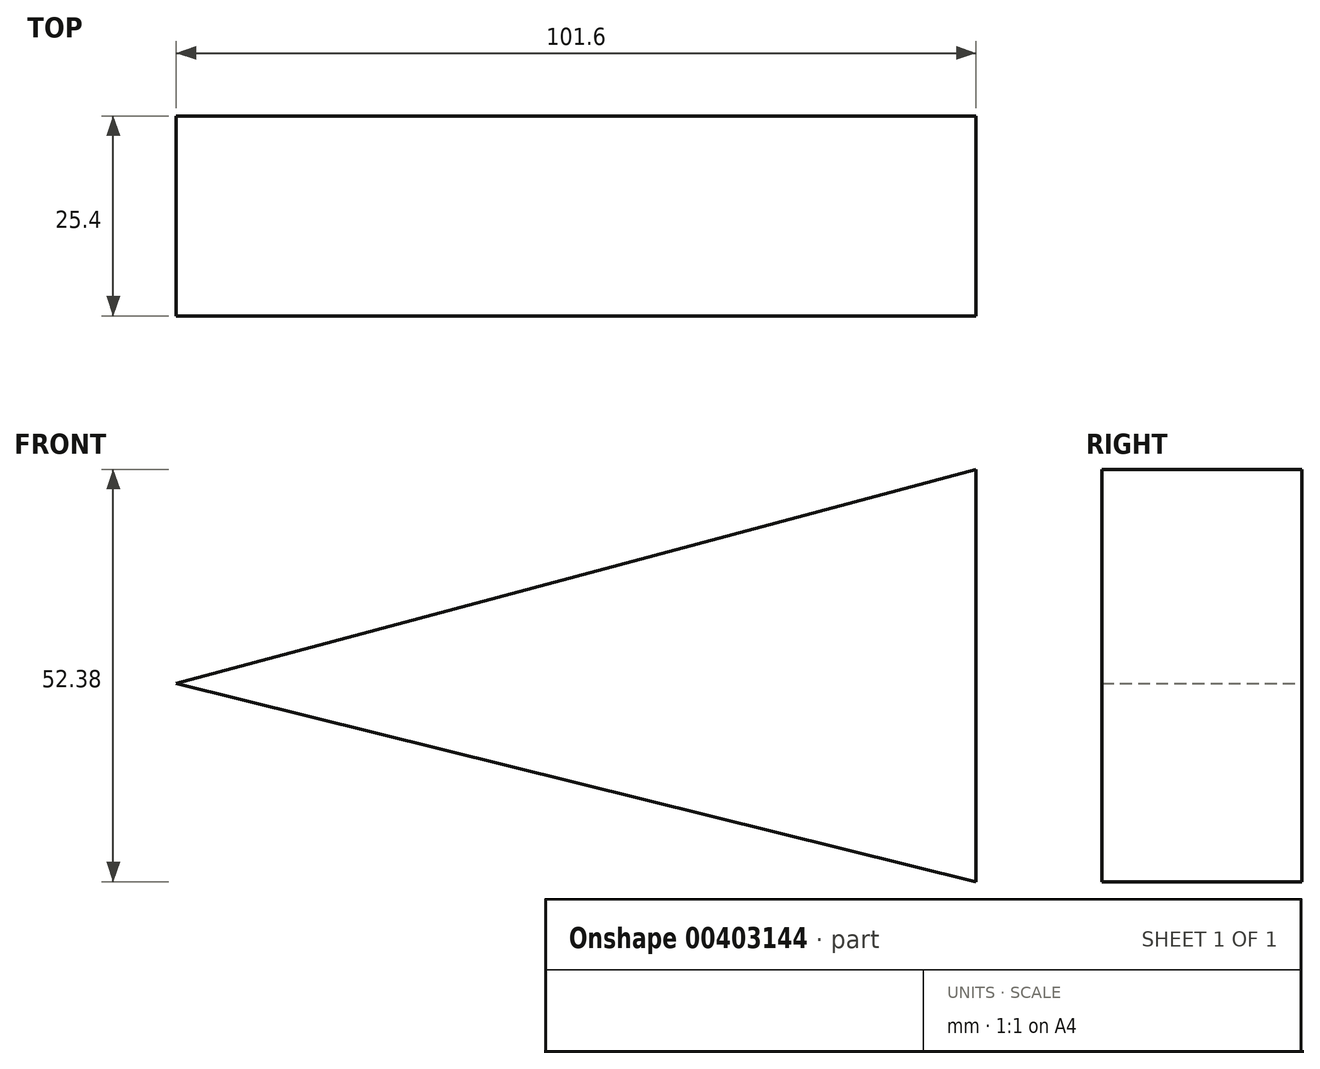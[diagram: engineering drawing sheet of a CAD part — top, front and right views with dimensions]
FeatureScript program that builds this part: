
annotation { "Feature Type Name" : "Feature", "Feature Type Description" : "" }
export const myFeature = defineFeature(function(context is Context, id is Id, definition is map)
    precondition{}
    {
        {
            var Q0;
            Q0=qCreatedBy(makeId("Front.planeOp"),FACE);
            var sketch = newSketch(context, id + "F0", { "sketchPlane" : qUnion([Q0])});
            skLineSegment(sketch, "E0", {"start": v(0, 0) * mm, "end": v(101.6, 27.22) * mm});
            skLineSegment(sketch, "E1", {"start": v(101.6, 27.22) * mm, "end": v(101.6, -25.16) * mm});
            skLineSegment(sketch, "E2", {"start": v(101.6, -25.16) * mm, "end": v(0, 0) * mm});
            skLineSegment(sketch, "E3", {"start": v(0, 0) * mm, "end": v(101.6, 0) * mm, "construction": true});
            skSolve(sketch);
        }
        {
            var Q0;
            Q0=makeQuery(id+"F0.imprint","IMPRINT",FACE,{"disambiguationData":[TD([[makeQuery(id+"F0.imprint","IMPRINT",EDGE,{"derivedFrom":sQuery(id+"F0.wireOp",EDGE,"E0")}),-1.0]])]});
            extrude(context, id + "F1", {"entities" : qUnion([Q0]), "depth" : 25.4 * mm, "offsetDistance" : 25.4 * mm});
        }
    });
